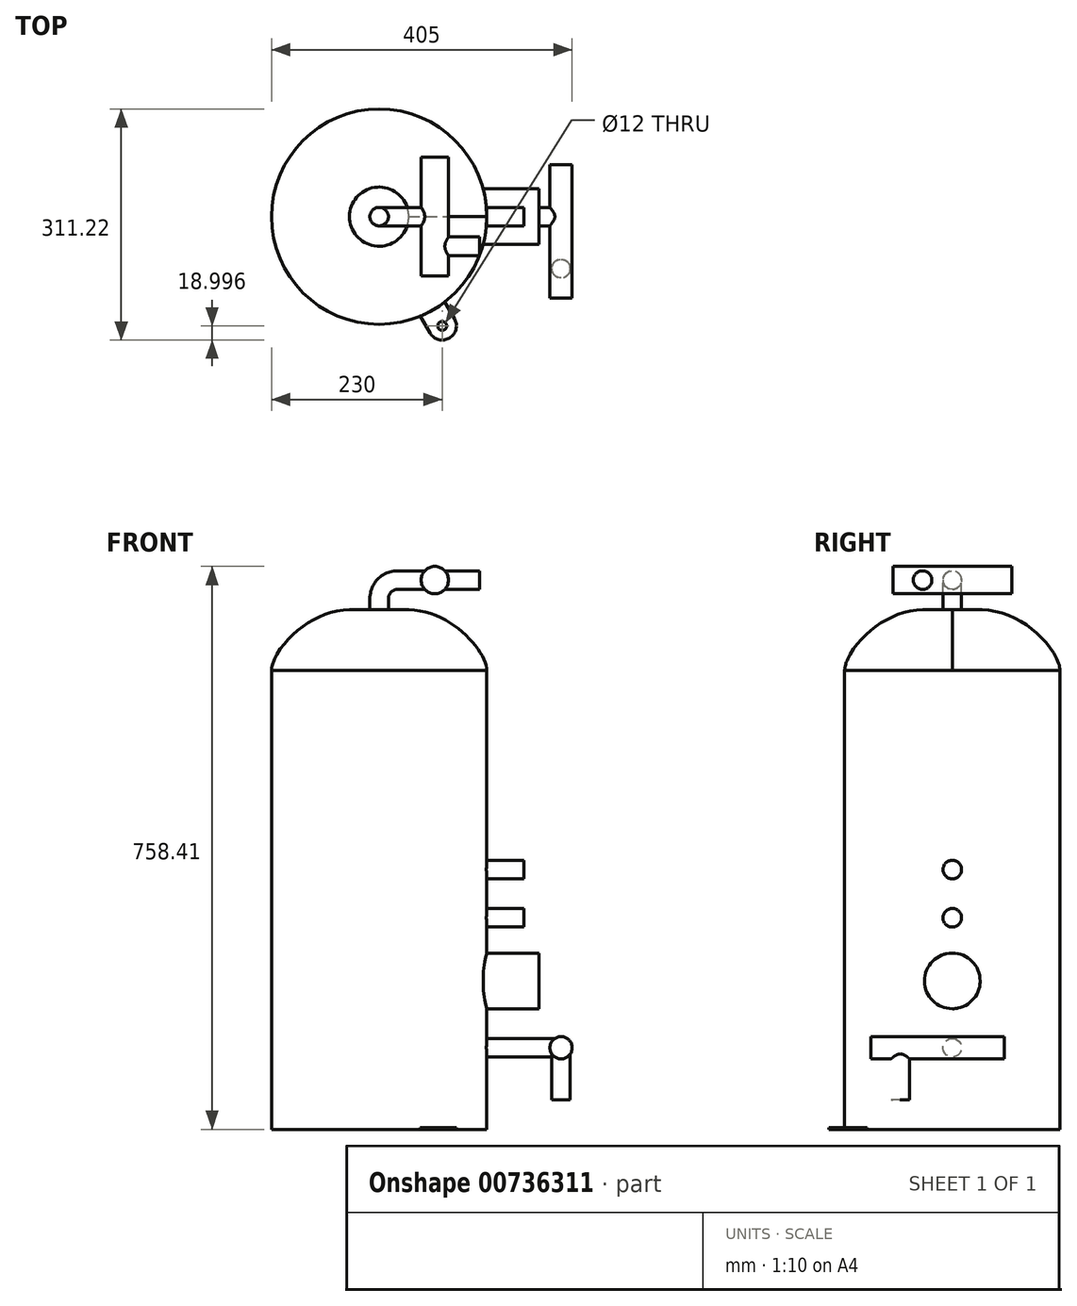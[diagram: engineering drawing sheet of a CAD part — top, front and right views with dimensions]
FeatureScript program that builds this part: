
annotation { "Feature Type Name" : "Feature", "Feature Type Description" : "" }
export const myFeature = defineFeature(function(context is Context, id is Id, definition is map)
    precondition{}
    {
        {
            var Q0;
            Q0=qCreatedBy(makeId("Front.planeOp"),FACE);
            var sketch = newSketch(context, id + "F0", { "sketchPlane" : qUnion([Q0])});
            skLineSegment(sketch, "E0", {"start": v(0, 0) * mm, "end": v(0, 700) * mm, "construction": true});
            skLineSegment(sketch, "E1", {"start": v(0, 0) * mm, "end": v(145, 0) * mm});
            skLineSegment(sketch, "E2", {"start": v(145, 0) * mm, "end": v(145, 617.97) * mm});
            skLineSegment(sketch, "E3", {"start": v(0, 700) * mm, "end": v(0, 700) * mm});
            skLineSegment(sketch, "E4", {"start": v(0, 700) * mm, "end": v(0, 0) * mm});
            skLineSegment(sketch, "E5", {"start": v(0, 700) * mm, "end": v(39.85, 700) * mm});
            skFitSpline(sketch, "E6", {"points": [v(39.85, 700) * mm, v(145, 617.97) * mm], "startDerivative": vector(177.62, -3.76) * mm, "endDerivative": vector(0.23, -75.54) * mm});
            skSolve(sketch);
        }
        {
            var Q0;
            Q0=makeQuery(id+"F0.imprint","IMPRINT",FACE,{"disambiguationData":[TD([[makeQuery(id+"F0.imprint","IMPRINT",EDGE,{"derivedFrom":sQuery(id+"F0.wireOp",EDGE,"E1")}),1.0]])]});
            var Q1;
            Q1=sQuery(id+"F0.wireOp",EDGE,"E4");
            revolve(context, id + "F1", {"surfaceOperationType" : NewSurfaceOperationType.NEW, "entities" : qUnion([Q0]), "axis" : qUnion([Q1]), "revolveType" : RevolveType.FULL});
        }
        {
            var Q0;
            Q0=qCreatedBy(makeId("Front.planeOp"),FACE);
            var sketch = newSketch(context, id + "F2", { "sketchPlane" : qUnion([Q0])});
            skLineSegment(sketch, "E7.bottom", {"start": v(135, 200) * mm, "end": v(215, 200) * mm});
            skLineSegment(sketch, "E7.top", {"start": v(135, 237.5) * mm, "end": v(215, 237.5) * mm});
            skLineSegment(sketch, "E7.left", {"start": v(135, 200) * mm, "end": v(135, 237.5) * mm});
            skLineSegment(sketch, "E7.right", {"start": v(215, 200) * mm, "end": v(215, 237.5) * mm});
            skLineSegment(sketch, "E8", {"start": v(145, 617.97) * mm, "end": v(145, 0) * mm, "construction": true});
            skLineSegment(sketch, "E9.bottom", {"start": v(135, 110) * mm, "end": v(245, 110) * mm});
            skLineSegment(sketch, "E9.top", {"start": v(135, 122.5) * mm, "end": v(245, 122.5) * mm});
            skLineSegment(sketch, "E9.left", {"start": v(135, 110) * mm, "end": v(135, 122.5) * mm});
            skLineSegment(sketch, "E9.right", {"start": v(245, 110) * mm, "end": v(245, 122.5) * mm});
            skLineSegment(sketch, "E10.bottom", {"start": v(135, 297.5) * mm, "end": v(195, 297.5) * mm});
            skLineSegment(sketch, "E10.top", {"start": v(135, 285) * mm, "end": v(195, 285) * mm});
            skLineSegment(sketch, "E10.left", {"start": v(135, 297.5) * mm, "end": v(135, 285) * mm});
            skLineSegment(sketch, "E10.right", {"start": v(195, 297.5) * mm, "end": v(195, 285) * mm});
            skLineSegment(sketch, "E11.bottom", {"start": v(135, 350) * mm, "end": v(195, 350) * mm});
            skLineSegment(sketch, "E11.top", {"start": v(135, 362.5) * mm, "end": v(195, 362.5) * mm});
            skLineSegment(sketch, "E11.left", {"start": v(135, 350) * mm, "end": v(135, 362.5) * mm});
            skLineSegment(sketch, "E11.right", {"start": v(195, 350) * mm, "end": v(195, 362.5) * mm});
            skSolve(sketch);
        }
        {
            var Q0;
            Q0=makeQuery(id+"F2.imprint","IMPRINT",FACE,{"disambiguationData":[TD([[makeQuery(id+"F2.imprint","IMPRINT",EDGE,{"derivedFrom":sQuery(id+"F2.wireOp",EDGE,"E9.bottom")}),1.0]])]});
            var Q1;
            Q1=sQuery(id+"F2.wireOp",EDGE,"E9.bottom");
            revolve(context, id + "F3", {"operationType" : NewBodyOperationType.ADD, "surfaceOperationType" : NewSurfaceOperationType.NEW, "entities" : qUnion([Q0]), "axis" : qUnion([Q1]), "revolveType" : RevolveType.FULL});
        }
        {
            var Q0;
            Q0=makeQuery(id+"F2.imprint","IMPRINT",FACE,{"disambiguationData":[TD([[makeQuery(id+"F2.imprint","IMPRINT",EDGE,{"derivedFrom":sQuery(id+"F2.wireOp",EDGE,"E7.bottom")}),1.0]])]});
            var Q1;
            Q1=sQuery(id+"F2.wireOp",EDGE,"E7.bottom");
            revolve(context, id + "F4", {"operationType" : NewBodyOperationType.ADD, "surfaceOperationType" : NewSurfaceOperationType.NEW, "entities" : qUnion([Q0]), "axis" : qUnion([Q1]), "revolveType" : RevolveType.FULL});
        }
        {
            var Q0;
            Q0=makeQuery(id+"F2.imprint","IMPRINT",FACE,{"disambiguationData":[TD([[makeQuery(id+"F2.imprint","IMPRINT",EDGE,{"derivedFrom":sQuery(id+"F2.wireOp",EDGE,"E10.bottom")}),-1.0]])]});
            var Q1;
            Q1=sQuery(id+"F2.wireOp",EDGE,"E10.top");
            revolve(context, id + "F5", {"operationType" : NewBodyOperationType.ADD, "surfaceOperationType" : NewSurfaceOperationType.NEW, "entities" : qUnion([Q0]), "axis" : qUnion([Q1]), "revolveType" : RevolveType.FULL});
        }
        {
            var Q0;
            Q0=makeQuery(id+"F2.imprint","IMPRINT",FACE,{"disambiguationData":[TD([[makeQuery(id+"F2.imprint","IMPRINT",EDGE,{"derivedFrom":sQuery(id+"F2.wireOp",EDGE,"E11.bottom")}),1.0]])]});
            var Q1;
            Q1=sQuery(id+"F2.wireOp",EDGE,"E11.bottom");
            revolve(context, id + "F6", {"operationType" : NewBodyOperationType.ADD, "surfaceOperationType" : NewSurfaceOperationType.NEW, "entities" : qUnion([Q0]), "axis" : qUnion([Q1]), "revolveType" : RevolveType.FULL});
        }
        {
            var Q0;
            Q0=qCreatedBy(makeId("Front.planeOp"),FACE);
            var sketch = newSketch(context, id + "F7", { "sketchPlane" : qUnion([Q0])});
            skLineSegment(sketch, "E12", {"start": v(0, 700) * mm, "end": v(0, 715) * mm});
            skLineSegment(sketch, "E13", {"start": v(25, 740) * mm, "end": v(75, 740) * mm});
            skLineSegment(sketch, "E14.0", {"start": v(-39.85, 700) * mm, "end": v(39.85, 700) * mm, "construction": true});
            skPoint(sketch, "E15.visualSharp", {"position": v(0, 740) * mm});
            skArc(sketch, "E15.filletArc", {"start": v(25, 740) * mm, "mid": v(7.32, 732.68) * mm, "end": v(0, 715) * mm});
            skSolve(sketch);
        }
        {
            var Q0;
            Q0=makeQuery(id+"F1.opRevolve","SWEPT_FACE",FACE,{"disambiguationData":[OSD([sQuery(id+"F0.wireOp",EDGE,"E5")])]});
            var sketch = newSketch(context, id + "F8", { "sketchPlane" : qUnion([Q0])});
            skCircle(sketch, "E16", {"center": v(0, 0) * mm, "radius": 12.5 * mm});
            skSolve(sketch);
        }
        {
            var Q0;
            Q0=makeQuery(id+"F8.imprint","IMPRINT",FACE,{"disambiguationData":[TD([[makeQuery(id+"F8.imprint","IMPRINT",EDGE,{"derivedFrom":sQuery(id+"F8.wireOp",EDGE,"E16")}),1.0]])]});
            var Q1;
            Q1=sQuery(id+"F8.wireOp",EDGE,"E16");
            var Q2;
            Q2=sQuery(id+"F7.wireOp",EDGE,"E12");
            var Q3;
            Q3=sQuery(id+"F7.wireOp",EDGE,"E15.filletArc");
            var Q4;
            Q4=sQuery(id+"F7.wireOp",EDGE,"E13");
            sweep(context, id + "F9", {"operationType" : NewBodyOperationType.ADD, "profiles" : qUnion([Q0]), "surfaceProfiles" : qUnion([Q1]), "path" : qUnion([Q2, Q3, Q4])});
        }
        {
            var Q0;
            Q0=qCreatedBy(makeId("Front.planeOp"),FACE);
            var sketch = newSketch(context, id + "F10", { "sketchPlane" : qUnion([Q0])});
            skLineSegment(sketch, "E17.0", {"start": v(75, 752.5) * mm, "end": v(75, 727.5) * mm, "construction": true});
            skCircle(sketch, "E18", {"center": v(75, 740) * mm, "radius": 18.41 * mm});
            skSolve(sketch);
        }
        {
            var Q0;
            Q0 = qSketchRegion(id + "F10", true);
            extrude(context, id + "F11", {"entities" : qUnion([Q0]), "operationType" : NewBodyOperationType.ADD, "endBound" : BoundingType.SYMMETRIC, "depth" : 160 * mm, "offsetDistance" : 25.4 * mm});
        }
        {
            var Q0;
            Q0=qCreatedBy(makeId("Right.planeOp"),FACE);
            var Q1;
            Q1=makeQuery(id+"F11.opExtrude","SWEPT_FACE",FACE,{"disambiguationData":[OSD([sQuery(id+"F10.wireOp",EDGE,"E18")])]});
            cPlane(context, id + "F12", {"entities" : qUnion([Q0, Q1]), "cplaneType" : CPlaneType.LINE_ANGLE, "offset" : 145 * mm, "angle" : 0 * degree, "width" : 152.4 * mm, "height" : 152.4 * mm});
        }
        {
            var Q0;
            Q0=makeQuery(id+"F11.opExtrude","SWEPT_FACE",FACE,{"disambiguationData":[OSD([sQuery(id+"F10.wireOp",EDGE,"E18")])]});
            var Q1;
            Q1=qCreatedBy(id+"F12.planeOp",FACE);
            cPlane(context, id + "F13", {"entities" : qUnion([Q0, Q1]), "cplaneType" : CPlaneType.LINE_ANGLE, "offset" : 25.4 * mm, "angle" : 90 * degree, "width" : 152.4 * mm, "height" : 152.4 * mm});
        }
        {
            var Q0;
            Q0=qCreatedBy(id+"F12.planeOp",FACE);
            var sketch = newSketch(context, id + "F14", { "sketchPlane" : qUnion([Q0])});
            skCircle(sketch, "E19", {"center": v(40, 740) * mm, "radius": 12.5 * mm});
            skSolve(sketch);
        }
        {
            var Q0;
            Q0 = qSketchRegion(id + "F14", true);
            extrude(context, id + "F15", {"entities" : qUnion([Q0]), "operationType" : NewBodyOperationType.ADD, "oppositeDirection" : true, "depth" : 60 * mm, "offsetDistance" : 25.4 * mm});
        }
        {
            var Q0;
            Q0=qCreatedBy(makeId("Front.planeOp"),FACE);
            var sketch = newSketch(context, id + "F16", { "sketchPlane" : qUnion([Q0])});
            skLineSegment(sketch, "E20.0", {"start": v(245, 97.5) * mm, "end": v(245, 122.5) * mm, "construction": true});
            skCircle(sketch, "E21", {"center": v(245, 110) * mm, "radius": 15 * mm});
            skSolve(sketch);
        }
        {
            var Q0;
            Q0 = qSketchRegion(id + "F16", true);
            extrude(context, id + "F17", {"entities" : qUnion([Q0]), "operationType" : NewBodyOperationType.ADD, "depth" : 110 * mm, "offsetDistance" : 25.4 * mm, "hasSecondDirection" : true, "secondDirectionOppositeDirection" : true, "secondDirectionDepth" : 70 * mm});
        }
        {
            var Q0;
            Q0=makeQuery(id+"F17.opExtrude","SWEPT_FACE",FACE,{"disambiguationData":[OSD([sQuery(id+"F16.wireOp",EDGE,"E21")])]});
            var Q1;
            Q1=qCreatedBy(makeId("Right.planeOp"),FACE);
            cPlane(context, id + "F18", {"entities" : qUnion([Q0, Q1]), "cplaneType" : CPlaneType.LINE_ANGLE, "offset" : 25.4 * mm, "angle" : 0 * degree, "width" : 152.4 * mm, "height" : 152.4 * mm});
        }
        {
            var Q0;
            Q0=makeQuery(id+"F17.opExtrude","SWEPT_FACE",FACE,{"disambiguationData":[OSD([sQuery(id+"F16.wireOp",EDGE,"E21")])]});
            var Q1;
            Q1=qCreatedBy(id+"F18.planeOp",FACE);
            cPlane(context, id + "F19", {"entities" : qUnion([Q0, Q1]), "cplaneType" : CPlaneType.LINE_ANGLE, "offset" : 25.4 * mm, "angle" : 90 * degree, "width" : 152.4 * mm, "height" : 152.4 * mm});
        }
        {
            var Q0;
            Q0=qCreatedBy(id+"F19.planeOp",FACE);
            var sketch = newSketch(context, id + "F20", { "sketchPlane" : qUnion([Q0])});
            skCircle(sketch, "E22", {"center": v(245, 70) * mm, "radius": 12.5 * mm});
            skSolve(sketch);
        }
        {
            var Q0;
            Q0 = qSketchRegion(id + "F20", true);
            extrude(context, id + "F21", {"entities" : qUnion([Q0]), "operationType" : NewBodyOperationType.ADD, "depth" : 70 * mm, "offsetDistance" : 25.4 * mm});
        }
        {
            var Q0;
            Q0=makeQuery(id+"F1.opRevolve","SWEPT_FACE",FACE,{"disambiguationData":[OSD([sQuery(id+"F0.wireOp",EDGE,"E1")])]});
            var sketch = newSketch(context, id + "F22", { "sketchPlane" : qUnion([Q0])});
            skArc(sketch, "E23", {"start": v(68.55, 156.72) * mm, "mid": v(94.5, 163.68) * mm, "end": v(101.45, 137.72) * mm});
            skLineSegment(sketch, "E24", {"start": v(85, 147.22) * mm, "end": v(0, 0) * mm, "construction": true});
            skLineSegment(sketch, "E25", {"start": v(68.55, 156.72) * mm, "end": v(55.42, 134) * mm});
            skLineSegment(sketch, "E26", {"start": v(101.45, 137.72) * mm, "end": v(88.33, 115) * mm});
            skPoint(sketch, "E27.visualSharp", {"position": v(14.05, 286.84) * mm});
            skCircle(sketch, "E28", {"center": v(85, 147.22) * mm, "radius": 6 * mm});
            skArc(sketch, "E29", {"start": v(88.33, 115) * mm, "mid": v(72.5, 125.57) * mm, "end": v(55.42, 134) * mm});
            skPoint(sketch, "E30.center", {"position": v(0, -14.54) * mm});
            skSolve(sketch);
        }
        {
            var Q0;
            Q0 = qSketchRegion(id + "F22", true);
            extrude(context, id + "F23", {"entities" : qUnion([Q0]), "oppositeDirection" : true, "depth" : 2 * mm, "offsetDistance" : 25.4 * mm});
        }
    });
